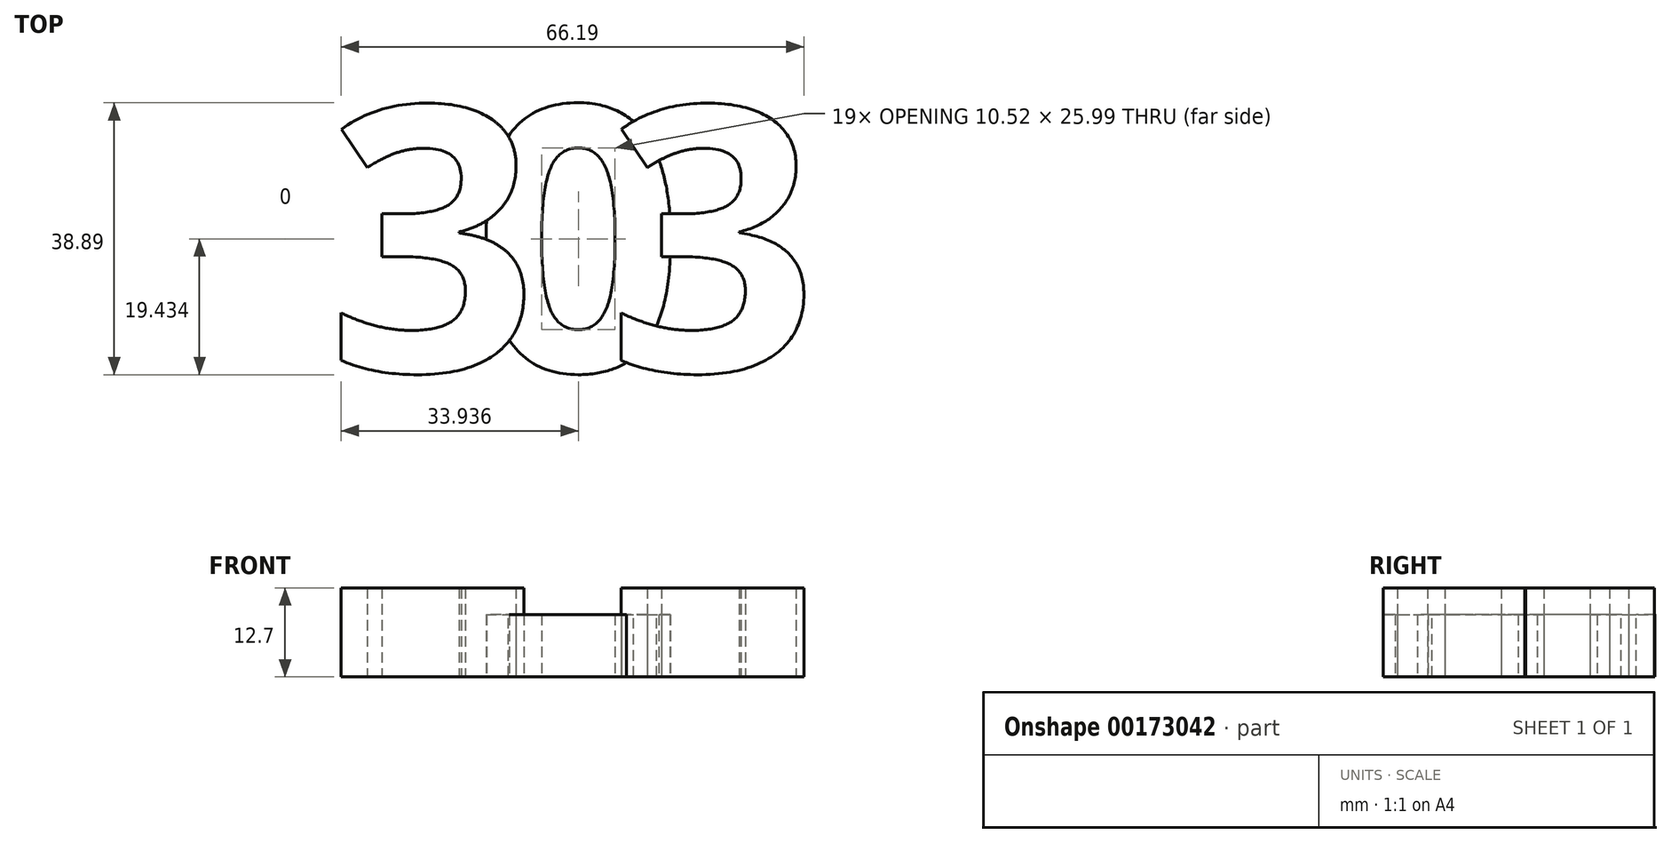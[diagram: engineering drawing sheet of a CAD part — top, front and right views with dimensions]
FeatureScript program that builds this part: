
annotation { "Feature Type Name" : "Feature", "Feature Type Description" : "" }
export const myFeature = defineFeature(function(context is Context, id is Id, definition is map)
    precondition{}
    {
        {
            var Q0;
            Q0=qCreatedBy(makeId("Top.planeOp"),FACE);
            var sketch = newSketch(context, id + "F0", { "sketchPlane" : qUnion([Q0])});
            skLineSegment(sketch, "E0.bottom", {"start": v(0, 0) * mm, "end": v(127, 0) * mm});
            skLineSegment(sketch, "E0.top", {"start": v(0, 50.8) * mm, "end": v(127, 50.8) * mm});
            skLineSegment(sketch, "E0.left", {"start": v(0, 0) * mm, "end": v(0, 50.8) * mm});
            skLineSegment(sketch, "E0.right", {"start": v(127, 0) * mm, "end": v(127, 50.8) * mm});
            skText(sketch, "E1", { "text": "3", "fontName": "OpenSans-Bold.ttf"});
            skText(sketch, "E2", { "text": "0", "fontName": "OpenSans-Bold.ttf"});
            skText(sketch, "E3", { "text": "3", "fontName": "OpenSans-Bold.ttf"});
            const initialGuessF0  = {"E1": [0.00635, 0.00635, 1, 0, 0.0381], "E2": [0.0272, 0.00635, 1, 0, 0.0381], "E3": [0.0464, 0.00635, 1, 0, 0.0381]};
            skSetInitialGuess(sketch, initialGuessF0);
            skSolve(sketch);
        }
        {
            var Q0;
            {var subQ9=sQuery(id+"F0.wireOp",EDGE,"E1.sketch_text.stroke-2");Q0=makeQuery(id+"F0.imprint","IMPRINT",FACE,{"disambiguationData":[TD([[makeQuery(id+"F0.imprint","IMPRINT",EDGE,{"derivedFrom":subQ9}),-1.0]])]});}
            var Q1;
            {var subQ0=sQuery(id+"F0.wireOp",EDGE,"E1.sketch_text.stroke-0");Q1=makeQuery(id+"F0.imprint","IMPRINT",FACE,{"disambiguationData":[TD([[makeQuery(id+"F0.imprint","IMPRINT",EDGE,{"derivedFrom":subQ0}),-1.0]])]});}
            var Q2;
            {var subQ5=sQuery(id+"F0.wireOp",EDGE,"E1.sketch_text.stroke-4");Q2=makeQuery(id+"F0.imprint","IMPRINT",FACE,{"disambiguationData":[TD([[makeQuery(id+"F0.imprint","IMPRINT",EDGE,{"derivedFrom":subQ5}),-1.0]])]});}
            var Q3;
            Q3=makeQuery(id+"F0.imprint","IMPRINT",FACE,{"disambiguationData":[TD([[makeQuery(id+"F0.imprint","IMPRINT",EDGE,{"derivedFrom":sQuery(id+"F0.wireOp",EDGE,"E3.sketch_text.stroke-0")}),-1.0]])]});
            var Q4;
            {var subQ0=sQuery(id+"F0.wireOp",EDGE,"E3.sketch_text.stroke-23");Q4=makeQuery(id+"F0.imprint","IMPRINT",FACE,{"disambiguationData":[TD([[makeQuery(id+"F0.imprint","IMPRINT",EDGE,{"derivedFrom":subQ0}),-1.0]])]});}
            var Q5;
            {var subQ0=sQuery(id+"F0.wireOp",EDGE,"E3.sketch_text.stroke-16");Q5=makeQuery(id+"F0.imprint","IMPRINT",FACE,{"disambiguationData":[TD([[makeQuery(id+"F0.imprint","IMPRINT",EDGE,{"derivedFrom":subQ0}),-1.0]])]});}
            var Q6;
            {var subQ0=sQuery(id+"F0.wireOp",EDGE,"E3.sketch_text.stroke-8");Q6=makeQuery(id+"F0.imprint","IMPRINT",FACE,{"disambiguationData":[TD([[makeQuery(id+"F0.imprint","IMPRINT",EDGE,{"derivedFrom":subQ0}),-1.0]])]});}
            extrude(context, id + "F1", {"entities" : qUnion([Q0, Q1, Q2, Q3, Q4, Q5, Q6]), "depth" : 12.7 * mm});
        }
        {
            var Q0;
            {var subQ33=sQuery(id+"F0.wireOp",EDGE,"E1.sketch_text.stroke-0");Q0=makeQuery(id+"F0.imprint","IMPRINT",FACE,{"disambiguationData":[TD([[makeQuery(id+"F0.imprint","IMPRINT",EDGE,{"derivedFrom":subQ33}),1.0]])]});}
            extrude(context, id + "F2", {"entities" : qUnion([Q0]), "depth" : 8.9 * mm});
        }
    });
